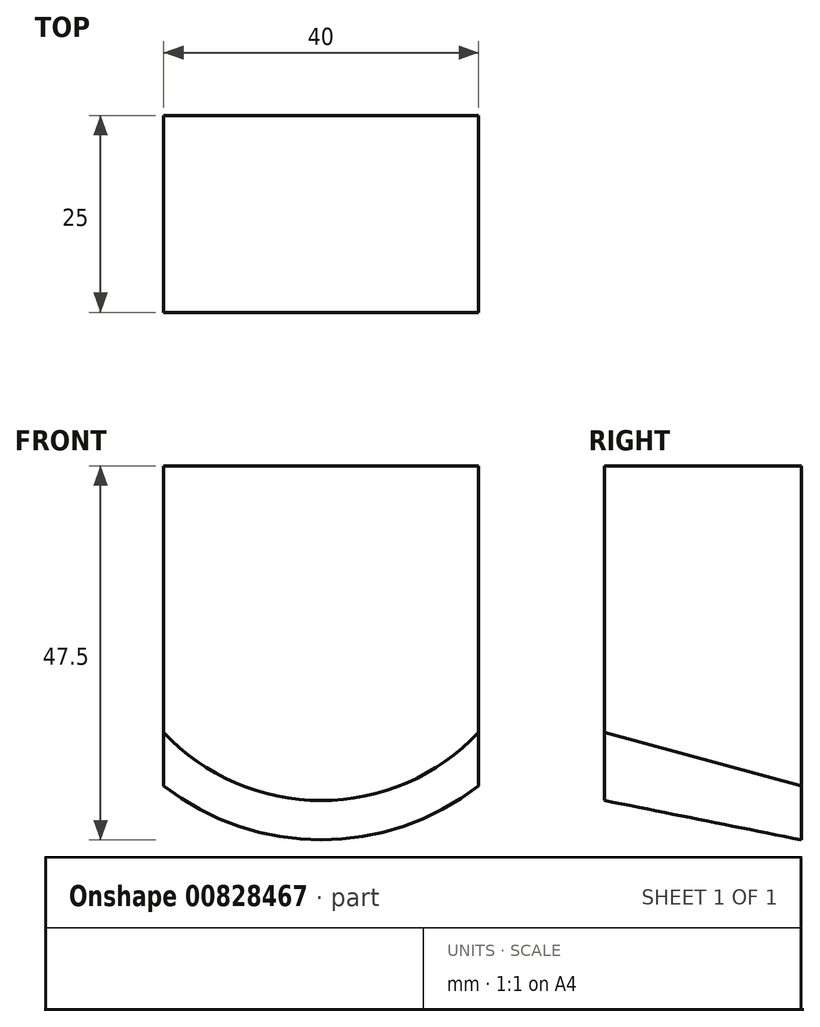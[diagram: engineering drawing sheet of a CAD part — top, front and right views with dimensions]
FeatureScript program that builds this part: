
annotation { "Feature Type Name" : "Feature", "Feature Type Description" : "" }
export const myFeature = defineFeature(function(context is Context, id is Id, definition is map)
    precondition{}
    {
        {
            var Q0;
            Q0=qCreatedBy(makeId("Front.planeOp"),FACE);
            var sketch = newSketch(context, id + "F0", { "sketchPlane" : qUnion([Q0])});
            skLineSegment(sketch, "E0", {"start": v(-20, -10) * mm, "end": v(-20, 15) * mm});
            skLineSegment(sketch, "E1", {"start": v(-20, 15) * mm, "end": v(20, 15) * mm});
            skLineSegment(sketch, "E2", {"start": v(20, 15) * mm, "end": v(20, -10) * mm});
            skLineSegment(sketch, "E3", {"start": v(-20, -10) * mm, "end": v(20, -10) * mm});
            skSolve(sketch);
        }
        {
            var Q0;
            Q0=makeQuery(id+"F0.imprint","IMPRINT",FACE,{"disambiguationData":[TD([[makeQuery(id+"F0.imprint","IMPRINT",EDGE,{"derivedFrom":sQuery(id+"F0.wireOp",EDGE,"E0")}),-1.0]])]});
            extrude(context, id + "F1", {"entities" : qUnion([Q0]), "depth" : 25 * mm, "offsetDistance" : 25 * mm});
        }
        {
            var Q0;
            Q0=makeQuery(id+"F1.opExtrude","CAP_FACE",FACE,{"disambiguationData":[OSD([sQuery(id+"F0.wireOp",EDGE,"E0"),sQuery(id+"F0.wireOp",EDGE,"E1"),sQuery(id+"F0.wireOp",EDGE,"E2"),sQuery(id+"F0.wireOp",EDGE,"E3")])],"isStart":false});
            var sketch = newSketch(context, id + "F2", { "sketchPlane" : qUnion([Q0])});
            skArc(sketch, "E4", {"start": v(-20, -18.87) * mm, "mid": v(0, -27.5) * mm, "end": v(20, -18.87) * mm});
            skLineSegment(sketch, "E5", {"start": v(-20, -10) * mm, "end": v(-20, -18.87) * mm});
            skLineSegment(sketch, "E6", {"start": v(-20, -10) * mm, "end": v(20, -10) * mm});
            skLineSegment(sketch, "E7", {"start": v(20, -10) * mm, "end": v(20, -18.87) * mm});
            skSolve(sketch);
        }
        {
            var Q0;
            Q0=makeQuery(id+"F1.opExtrude","CAP_FACE",FACE,{"disambiguationData":[OSD([sQuery(id+"F0.wireOp",EDGE,"E0"),sQuery(id+"F0.wireOp",EDGE,"E1"),sQuery(id+"F0.wireOp",EDGE,"E2"),sQuery(id+"F0.wireOp",EDGE,"E3")])],"isStart":true});
            var sketch = newSketch(context, id + "F3", { "sketchPlane" : qUnion([Q0])});
            skArc(sketch, "E8", {"start": v(-20, -25.62) * mm, "mid": v(0, -32.5) * mm, "end": v(20, -25.62) * mm});
            skLineSegment(sketch, "E9", {"start": v(-20, -10) * mm, "end": v(-20, -25.62) * mm});
            skLineSegment(sketch, "E10", {"start": v(-20, -10) * mm, "end": v(20, -10) * mm});
            skLineSegment(sketch, "E11", {"start": v(20, -10) * mm, "end": v(20, -25.62) * mm});
            skSolve(sketch);
        }
        {
            var Q1;
            Q1 = qSketchRegion(id + "F3", true);
            var Q2;
            Q2 = qSketchRegion(id + "F2", true);
            loft(context, id + "F4", {"operationType" : NewBodyOperationType.ADD, "sheetProfilesArray" : [{ "sheetProfileEntities" : qUnion([Q1]) }, { "sheetProfileEntities" : qUnion([Q2]) }]});
        }
    });
